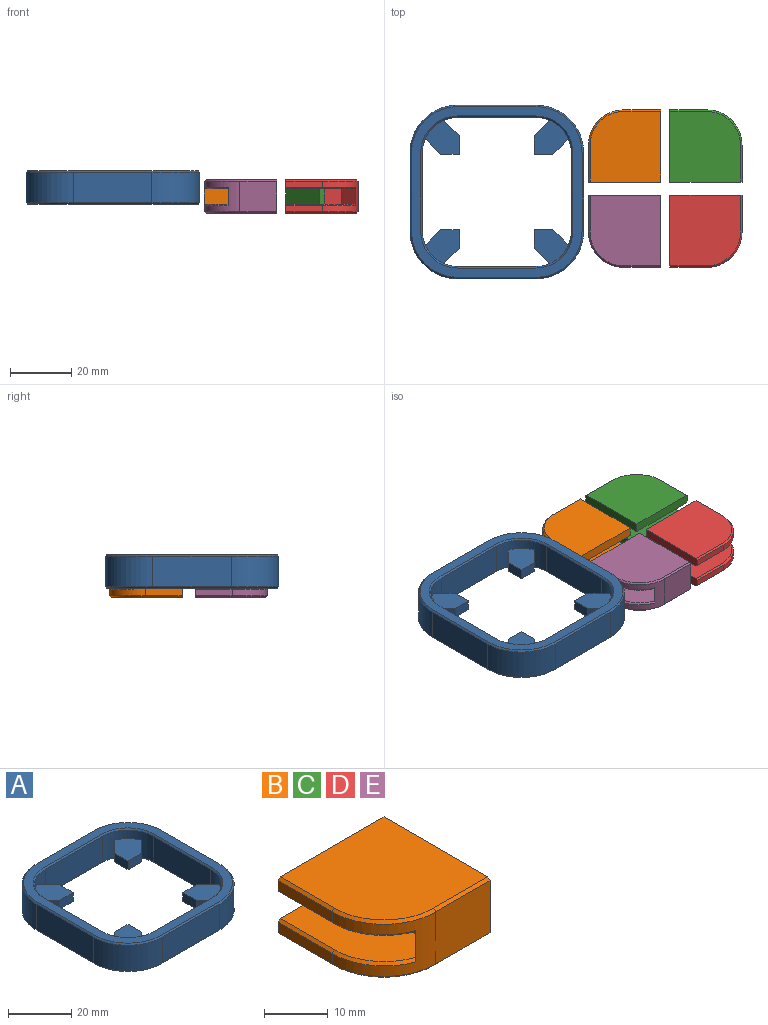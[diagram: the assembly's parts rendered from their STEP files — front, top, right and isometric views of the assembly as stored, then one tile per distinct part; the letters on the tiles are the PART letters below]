
ASSEMBLY  parts=5 mates=7
PART A: 74 faces, bbox 56.5x56.5x11 mm
  f0: plane 25.5x10mm, normal (-1,0,0), area 255mm2, adj f38,f41,f61,f69
  f1: plane 25.5x10mm, normal (0,-1,0), area 255mm2, adj f38,f39,f65,f73
  f2: plane 25.5x10mm, normal (1,0,0), area 255mm2, adj f39,f40,f62,f70
  f3: plane 25.5x10mm, normal (0,1,0), area 255mm2, adj f10,f13,f46,f54
  f4: plane 25.5x10mm, normal (1,0,0), area 255mm2, adj f10,f11,f49,f57
  f5: plane 25.5x10mm, normal (0,-1,0), area 255mm2, adj f11,f12,f45,f53
  f6: plane 25.5x10mm, normal (-1,0,0), area 255mm2, adj f12,f13,f42,f50
  f7: plane 25.5x10mm, normal (0,1,0), area 255mm2, adj f40,f41,f58,f66
  f8: plane 55.5x55.5mm, normal (0,0,1), area 560.5mm2, adj f50,f51,f52,f53,f54,f55,f56,f57
  f9: plane 55.5x55.5mm, normal (0,0,-1), area 560.5mm2, adj f42,f43,f44,f45,f46,f47,f48,f49
  f10: cylinder r=11.5mm len=11.5mm, axis (0,0,1), area 151.1mm2, adj f3,f4,f32,f33,f34,f35,f48,f56
  f11: cylinder r=11.5mm len=11.5mm, axis (0,0,-1), area 151.1mm2, adj f4,f5,f28,f29,f30,f31,f47,f55
  f12: cylinder r=11.5mm len=11.5mm, axis (0,0,1), area 151.1mm2, adj f5,f6,f22,f23,f24,f25,f43,f51
  f13: cylinder r=11.5mm len=11.5mm, axis (0,0,-1), area 151.1mm2, adj f3,f6,f16,f17,f18,f19,f44,f52
  f14: plane 6x3.4mm, normal (0,1,0), area 20.4mm2, adj f15,f16,f17,f19
  f15: plane 6x3.4mm, normal (-1,0,0), area 20.4mm2, adj f14,f16,f17,f18
  f16: plane 11.06x11.06mm, normal (0,0,-1), area 83.3mm2, adj f13,f14,f15,f18,f19
  f17: plane 11.06x11.06mm, normal (0,0,1), area 83.3mm2, adj f13,f14,f15,f18,f19
  f18: plane 5.06x5.06mm, normal (-0.71,-0.71,0), area 24.3mm2, adj f13,f15,f16,f17
  f19: plane 5.06x5.06mm, normal (0.71,0.71,0), area 24.3mm2, adj f13,f14,f16,f17
  f20: plane 6x3.4mm, normal (-1,0,0), area 20.4mm2, adj f21,f22,f23,f25
  f21: plane 6x3.4mm, normal (0,-1,0), area 20.4mm2, adj f20,f22,f23,f24
  f22: plane 11.06x11.06mm, normal (0,0,-1), area 83.3mm2, adj f12,f20,f21,f24,f25
  f23: plane 11.06x11.06mm, normal (0,0,1), area 83.3mm2, adj f12,f20,f21,f24,f25
  f24: plane 5.06x5.06mm, normal (0.71,-0.71,0), area 24.3mm2, adj f12,f21,f22,f23
  f25: plane 5.06x5.06mm, normal (-0.71,0.71,0), area 24.3mm2, adj f12,f20,f22,f23
  f26: plane 6x3.4mm, normal (0,-1,0), area 20.4mm2, adj f27,f28,f29,f31
  f27: plane 6x3.4mm, normal (1,0,0), area 20.4mm2, adj f26,f28,f29,f30
  f28: plane 11.06x11.06mm, normal (0,0,-1), area 83.3mm2, adj f11,f26,f27,f30,f31
  f29: plane 11.06x11.06mm, normal (0,0,1), area 83.3mm2, adj f11,f26,f27,f30,f31
  f30: plane 5.06x5.06mm, normal (0.71,0.71,0), area 24.3mm2, adj f11,f27,f28,f29
  f31: plane 5.06x5.06mm, normal (-0.71,-0.71,0), area 24.3mm2, adj f11,f26,f28,f29
  f32: plane 5.06x5.06mm, normal (0.71,-0.71,0), area 24.3mm2, adj f10,f34,f35,f36
  f33: plane 5.06x5.06mm, normal (-0.71,0.71,0), area 24.3mm2, adj f10,f34,f35,f37
  f34: plane 11.06x11.06mm, normal (0,0,1), area 83.3mm2, adj f10,f32,f33,f36,f37
  f35: plane 11.06x11.06mm, normal (0,0,-1), area 83.3mm2, adj f10,f32,f33,f36,f37
  f36: plane 6x3.4mm, normal (1,0,0), area 20.4mm2, adj f32,f34,f35,f37
  f37: plane 6x3.4mm, normal (0,1,0), area 20.4mm2, adj f33,f34,f35,f36
  f38: cylinder r=15.5mm len=15.5mm, axis (0,0,-1), area 243.5mm2, adj f0,f1,f63,f71
  f39: cylinder r=15.5mm len=15.5mm, axis (0,0,1), area 243.5mm2, adj f1,f2,f64,f72
  f40: cylinder r=15.5mm len=15.5mm, axis (0,0,-1), area 243.5mm2, adj f2,f7,f60,f68
  f41: cylinder r=15.5mm len=15.5mm, axis (0,0,1), area 243.5mm2, adj f0,f7,f59,f67
  f42: plane 25.5x0.5mm, normal (-0.71,0,-0.71), area 18mm2, adj f6,f9,f43,f44
  f43: cone r=12mm half-angle=45deg, axis (0,0,-1), area 13.1mm2, adj f9,f12,f42,f45
  f44: cone r=12mm half-angle=45deg, axis (0,0,-1), area 13.1mm2, adj f9,f13,f42,f46
  f45: plane 25.5x0.5mm, normal (0,-0.71,-0.71), area 18mm2, adj f5,f9,f43,f47
  f46: plane 25.5x0.5mm, normal (0,0.71,-0.71), area 18mm2, adj f3,f9,f44,f48
  f47: cone r=12mm half-angle=45deg, axis (0,0,-1), area 13.1mm2, adj f9,f11,f45,f49
  f48: cone r=12mm half-angle=45deg, axis (0,0,-1), area 13.1mm2, adj f9,f10,f46,f49
  f49: plane 25.5x0.5mm, normal (0.71,0,-0.71), area 18mm2, adj f4,f9,f47,f48
  f50: plane 25.5x0.5mm, normal (-0.71,0,0.71), area 18mm2, adj f6,f8,f51,f52
  f51: cone r=12mm half-angle=45deg, axis (0,0,1), area 13.1mm2, adj f8,f12,f50,f53
  f52: cone r=12mm half-angle=45deg, axis (0,0,1), area 13.1mm2, adj f8,f13,f50,f54
  f53: plane 25.5x0.5mm, normal (0,-0.71,0.71), area 18mm2, adj f5,f8,f51,f55
  f54: plane 25.5x0.5mm, normal (0,0.71,0.71), area 18mm2, adj f3,f8,f52,f56
  f55: cone r=12mm half-angle=45deg, axis (0,0,1), area 13.1mm2, adj f8,f11,f53,f57
  f56: cone r=12mm half-angle=45deg, axis (0,0,1), area 13.1mm2, adj f8,f10,f54,f57
  f57: plane 25.5x0.5mm, normal (0.71,0,0.71), area 18mm2, adj f4,f8,f55,f56
  f58: plane 25.5x0.5mm, normal (0,0.71,-0.71), area 18mm2, adj f7,f9,f59,f60
  f59: cone r=15mm half-angle=45deg, axis (0,0,1), area 16.9mm2, adj f9,f41,f58,f61
  f60: cone r=15mm half-angle=45deg, axis (0,0,1), area 16.9mm2, adj f9,f40,f58,f62
  f61: plane 25.5x0.5mm, normal (-0.71,0,-0.71), area 18mm2, adj f0,f9,f59,f63
  f62: plane 25.5x0.5mm, normal (0.71,0,-0.71), area 18mm2, adj f2,f9,f60,f64
  f63: cone r=15mm half-angle=45deg, axis (0,0,1), area 16.9mm2, adj f9,f38,f61,f65
  f64: cone r=15mm half-angle=45deg, axis (0,0,1), area 16.9mm2, adj f9,f39,f62,f65
  f65: plane 25.5x0.5mm, normal (0,-0.71,-0.71), area 18mm2, adj f1,f9,f63,f64
  f66: plane 25.5x0.5mm, normal (0,0.71,0.71), area 18mm2, adj f7,f8,f67,f68
  f67: cone r=15mm half-angle=45deg, axis (0,0,-1), area 16.9mm2, adj f8,f41,f66,f69
  f68: cone r=15mm half-angle=45deg, axis (0,0,-1), area 16.9mm2, adj f8,f40,f66,f70
  f69: plane 25.5x0.5mm, normal (-0.71,0,0.71), area 18mm2, adj f0,f8,f67,f71
  f70: plane 25.5x0.5mm, normal (0.71,0,0.71), area 18mm2, adj f2,f8,f68,f72
  f71: cone r=15mm half-angle=45deg, axis (0,0,-1), area 16.9mm2, adj f8,f38,f69,f73
  f72: cone r=15mm half-angle=45deg, axis (0,0,-1), area 16.9mm2, adj f8,f39,f70,f73
  f73: plane 25.5x0.5mm, normal (0,-0.71,0.71), area 18mm2, adj f1,f8,f71,f72
PART B: 25 faces, bbox 23.5x23.5x11 mm
  f0: plane 12x10mm, normal (0,-1,0), area 120mm2, adj f1,f8,f9,f14,f17,f20
  f1: plane 23.5x3mm, normal (1,0,0), area 70.4mm2, adj f0,f2,f4,f5,f20
  f2: plane 23.5x3mm, normal (0,1,0), area 70.2mm2, adj f1,f3,f4,f5,f18,f23
  f3: plane 12x2mm, normal (-1,0,0), area 24mm2, adj f2,f14,f18,f23
  f4: plane 23x23mm, normal (0,0,1), area 503mm2, adj f1,f2,f18,f19,f20
  f5: plane 23.5x23mm, normal (0,0,-1), area 436.3mm2, adj f1,f2,f6,f7,f8,f23,f24
  f6: plane 5.5x5mm, normal (-1,0,0), area 27.5mm2, adj f5,f7,f8,f13
  f7: plane 6.01x4.85mm, normal (-0.71,0.71,0), area 34.5mm2, adj f5,f6,f13,f14,f22,f24
  f8: plane 11x11mm, normal (0.71,0.71,0), area 77.8mm2, adj f0,f5,f6,f13
  f9: plane 23.5x3mm, normal (1,0,0), area 70.4mm2, adj f0,f10,f12,f13,f17
  f10: plane 23.5x3mm, normal (0,1,0), area 70.2mm2, adj f9,f11,f12,f13,f15,f21
  f11: plane 12x2mm, normal (-1,0,0), area 24mm2, adj f10,f14,f15,f21
  f12: plane 23x23mm, normal (0,0,-1), area 503mm2, adj f9,f10,f15,f16,f17
  f13: plane 23.5x23mm, normal (0,0,1), area 436.3mm2, adj f6,f7,f8,f9,f10,f21,f22
  f14: cylinder r=11.5mm len=11.5mm, axis (0,0,-1), area 95.7mm2, adj f0,f3,f7,f11,f16,f19,f22,f24
  f15: plane 12x0.5mm, normal (-0.71,0,-0.71), area 8.5mm2, adj f10,f11,f12,f16
  f16: cone r=11mm half-angle=45deg, axis (0,0,1), area 12.5mm2, adj f12,f14,f15,f17
  f17: plane 12x0.5mm, normal (0,-0.71,-0.71), area 8.5mm2, adj f0,f9,f12,f16
  f18: plane 12x0.5mm, normal (-0.71,0,0.71), area 8.5mm2, adj f2,f3,f4,f19
  f19: cone r=11mm half-angle=45deg, axis (0,0,-1), area 12.5mm2, adj f4,f14,f18,f20
  f20: plane 12x0.5mm, normal (0,-0.71,0.71), area 8.5mm2, adj f0,f1,f4,f19
  f21: plane 12x0.5mm, normal (-0.71,0,0.71), area 8.5mm2, adj f10,f11,f13,f22
  f22: cone r=11mm half-angle=45deg, axis (0,0,-1), area 9.9mm2, adj f7,f13,f14,f21
  f23: plane 12x0.5mm, normal (-0.71,0,-0.71), area 8.5mm2, adj f2,f3,f5,f24
  f24: cone r=11mm half-angle=45deg, axis (0,0,1), area 9.9mm2, adj f5,f7,f14,f23
PART C: same geometry as B
PART D: same geometry as B
PART E: same geometry as B
PLACE A t=(-12.3,2.95,9.58)mm fixed
PLACE B rot(axis=(0,0,-1),90deg) t=(41.05,29.68,9.11)mm
PLACE C rot(axis=(0,0,1),180deg) t=(67.52,6.18,9.11)mm
PLACE D rot(axis=(0,0,1),90deg) t=(44.02,-21.58,9.11)mm
PLACE E rot(axis=(0,0,1),0deg) t=(17.55,1.92,9.11)mm
MATE planar E.f3 <-> B.f0  axis (-1,0,0) through (17.55,-4.08,10.61)mm
MATE planar E.f12 <-> C.f12  axis (0,0,-1) through (30.02,-9.12,1.11)mm
MATE parallel A.f29 <-> B.f4  axis (0,0,1) through (-29.47,20.12,11.28)mm
MATE planar E.f4 <-> B.f4  axis (0,0,1) through (30.02,-9.12,12.11)mm
MATE planar E.f4 <-> D.f4  axis (0,0,1) through (30.02,-9.12,12.11)mm
MATE planar D.f0 <-> C.f3  axis (1,0,0) through (67.52,-4.08,6.61)mm
MATE planar B.f3 <-> C.f0  axis (0,1,0) through (35.05,29.68,10.61)mm
